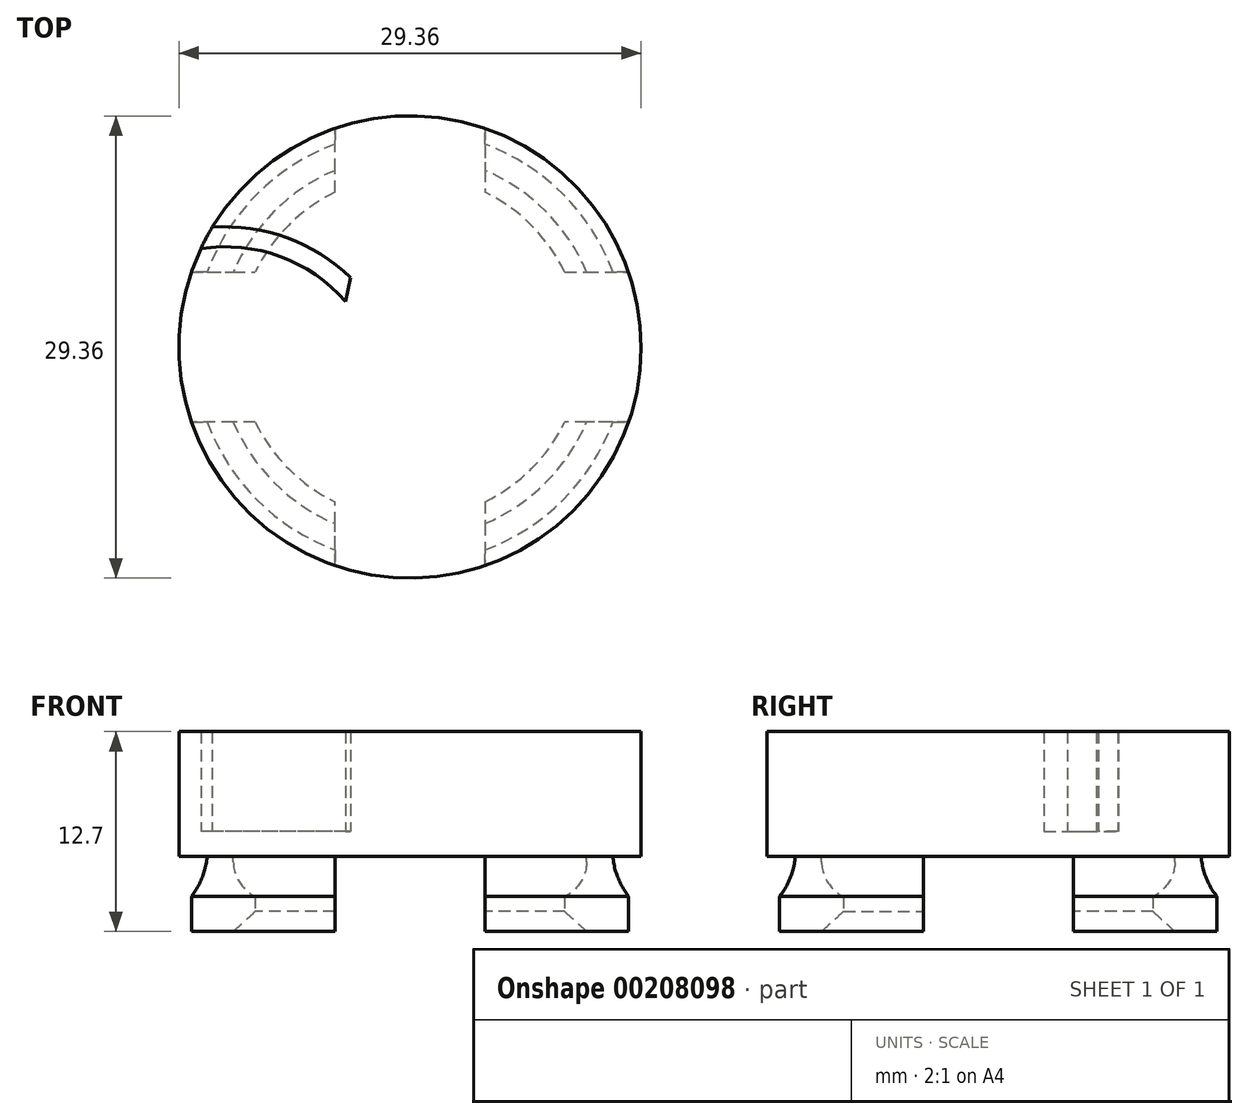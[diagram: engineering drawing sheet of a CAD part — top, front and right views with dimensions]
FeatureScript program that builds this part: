
annotation { "Feature Type Name" : "Feature", "Feature Type Description" : "" }
export const myFeature = defineFeature(function(context is Context, id is Id, definition is map)
    precondition{}
    {
        {
            var Q0;
            Q0=qCreatedBy(makeId("Top.planeOp"),FACE);
            var sketch = newSketch(context, id + "F0", { "sketchPlane" : qUnion([Q0])});
            skCircle(sketch, "E0", {"center": v(0, 0) * mm, "radius": 10.92 * mm});
            skCircle(sketch, "E1", {"center": v(0, 0) * mm, "radius": 14.68 * mm});
            skSolve(sketch);
        }
        {
            var Q0;
            Q0=makeQuery(id+"F0.imprint","IMPRINT",FACE,{"disambiguationData":[TD([[makeQuery(id+"F0.imprint","IMPRINT",EDGE,{"derivedFrom":sQuery(id+"F0.wireOp",EDGE,"E0")}),-1.0]])]});
            extrude(context, id + "F1", {"entities" : qUnion([Q0]), "depth" : 4.76 * mm});
        }
        {
            var Q0;
            Q0=makeQuery(id+"F1.opExtrude","CAP_FACE",FACE,{"disambiguationData":[OSD([sQuery(id+"F0.wireOp",EDGE,"E0"),sQuery(id+"F0.wireOp",EDGE,"E1")])],"isStart":false});
            var sketch = newSketch(context, id + "F2", { "sketchPlane" : qUnion([Q0])});
            skCircle(sketch, "E2", {"center": v(0, 0) * mm, "radius": 14.68 * mm});
            skSolve(sketch);
        }
        {
            var Q0;
            Q0 = qSketchRegion(id + "F2", true);
            extrude(context, id + "F3", {"entities" : qUnion([Q0]), "operationType" : NewBodyOperationType.ADD, "depth" : 1.59 * mm});
        }
        {
            var Q0;
            Q0=makeQuery(id+"F3.opExtrude","CAP_FACE",FACE,{"disambiguationData":[OSD([sQuery(id+"F2.wireOp",EDGE,"E2")])],"isStart":false});
            var sketch = newSketch(context, id + "F4", { "sketchPlane" : qUnion([Q0])});
            skLineSegment(sketch, "E3", {"start": v(1.24, 2.59) * mm, "end": v(-12.56, 7.6) * mm, "construction": true});
            skLineSegment(sketch, "E4", {"start": v(-14.5, -11.42) * mm, "end": v(-8.16, 6) * mm, "construction": true});
            skLineSegment(sketch, "E5", {"start": v(-13.28, 6.25) * mm, "end": v(-3.22, 2.59) * mm, "construction": true});
            skArc(sketch, "E6", {"start": v(-13.28, 6.25) * mm, "mid": v(-8.26, 5.76) * mm, "end": v(-4.09, 2.9) * mm});
            skArc(sketch, "E7", {"start": v(-12.56, 7.6) * mm, "mid": v(-7.82, 6.95) * mm, "end": v(-3.77, 4.41) * mm});
            skLineSegment(sketch, "E8", {"start": v(-4.09, 2.9) * mm, "end": v(-3.77, 4.41) * mm});
            skArc(sketch, "E9", {"start": v(-12.56, 7.6) * mm, "mid": v(-12.94, 6.94) * mm, "end": v(-13.28, 6.25) * mm});
            skSolve(sketch);
        }
        {
            var Q0;
            Q0=makeQuery(id+"F4.imprint","IMPRINT",FACE,{"disambiguationData":[TD([[makeQuery(id+"F4.imprint","IMPRINT",EDGE,{"derivedFrom":sQuery(id+"F4.wireOp",EDGE,"E6")}),1.0]])]});
            extrude(context, id + "F5", {"entities" : qUnion([Q0]), "operationType" : NewBodyOperationType.ADD, "depth" : 6.35 * mm});
        }
        {
            var Q0;
            Q0=qCreatedBy(makeId("Front.planeOp"),FACE);
            var sketch = newSketch(context, id + "F6", { "sketchPlane" : qUnion([Q0])});
            skLineSegment(sketch, "E10", {"start": v(0, 0) * mm, "end": v(0, 45.47) * mm, "construction": true});
            skSolve(sketch);
        }
        {
            var Q0;
            Q0=makeQuery(id+"F1.opExtrude","CAP_FACE",FACE,{"disambiguationData":[OSD([sQuery(id+"F0.wireOp",EDGE,"E0"),sQuery(id+"F0.wireOp",EDGE,"E1")])],"isStart":true});
            var sketch = newSketch(context, id + "F7", { "sketchPlane" : qUnion([Q0])});
            skLineSegment(sketch, "E11", {"start": v(-15.88, 4.76) * mm, "end": v(-15.88, -4.76) * mm});
            skLineSegment(sketch, "E12", {"start": v(-15.88, -4.76) * mm, "end": v(-4.76, -4.76) * mm});
            skLineSegment(sketch, "E13", {"start": v(-4.76, -4.76) * mm, "end": v(-4.76, -15.88) * mm});
            skLineSegment(sketch, "E14", {"start": v(-4.76, -15.88) * mm, "end": v(4.76, -15.88) * mm});
            skLineSegment(sketch, "E15", {"start": v(4.76, -15.88) * mm, "end": v(4.76, -4.76) * mm});
            skLineSegment(sketch, "E16", {"start": v(4.76, -4.76) * mm, "end": v(15.88, -4.76) * mm});
            skLineSegment(sketch, "E17", {"start": v(15.88, -4.76) * mm, "end": v(15.88, 4.76) * mm});
            skLineSegment(sketch, "E18", {"start": v(15.88, 4.76) * mm, "end": v(4.76, 4.76) * mm});
            skLineSegment(sketch, "E19", {"start": v(4.76, 4.76) * mm, "end": v(4.76, 15.88) * mm});
            skLineSegment(sketch, "E20", {"start": v(4.76, 15.87) * mm, "end": v(-4.76, 15.87) * mm});
            skLineSegment(sketch, "E21", {"start": v(-4.76, 15.88) * mm, "end": v(-4.76, 4.76) * mm});
            skLineSegment(sketch, "E22", {"start": v(-4.76, 4.76) * mm, "end": v(-15.88, 4.76) * mm});
            skLineSegment(sketch, "E23", {"start": v(0, 15.88) * mm, "end": v(0, -15.88) * mm, "construction": true});
            skLineSegment(sketch, "E24", {"start": v(-15.88, 0) * mm, "end": v(15.88, 0) * mm, "construction": true});
            skSolve(sketch);
        }
        {
            var Q0;
            Q0 = qSketchRegion(id + "F7", true);
            var Q1;
            Q1=makeQuery(id+"F3.opExtrude","CAP_FACE",FACE,{"disambiguationData":[OSD([sQuery(id+"F2.wireOp",EDGE,"E2")])],"isStart":true});
            extrude(context, id + "F8", {"entities" : qUnion([Q0]), "operationType" : NewBodyOperationType.REMOVE, "endBound" : BoundingType.UP_TO_SURFACE, "oppositeDirection" : true, "endBoundEntityFace" : qUnion([Q1]), "depth" : 25.4 * mm});
        }
        {
            var Q0;
            Q0=makeQuery(id+"F8.boolean.opBoolean","MERGE",FACE,{"derivedFrom":[makeQuery(id+"F3.opExtrude","CAP_FACE",FACE,{"disambiguationData":[OSD([sQuery(id+"F2.wireOp",EDGE,"E2")])],"isStart":true})],"fromTools":[makeQuery(id+"F8.opExtrude","CAP_FACE",FACE,{"disambiguationData":[OSD([sQuery(id+"F7.wireOp",EDGE,"E11"),sQuery(id+"F7.wireOp",EDGE,"E12"),sQuery(id+"F7.wireOp",EDGE,"E13"),sQuery(id+"F7.wireOp",EDGE,"E14"),sQuery(id+"F7.wireOp",EDGE,"E15"),sQuery(id+"F7.wireOp",EDGE,"E16"),sQuery(id+"F7.wireOp",EDGE,"E17"),sQuery(id+"F7.wireOp",EDGE,"E18"),sQuery(id+"F7.wireOp",EDGE,"E19"),sQuery(id+"F7.wireOp",EDGE,"E20"),sQuery(id+"F7.wireOp",EDGE,"E21"),sQuery(id+"F7.wireOp",EDGE,"E22")])],"isStart":false})]});
            var sketch = newSketch(context, id + "F9", { "sketchPlane" : qUnion([Q0])});
            skCircle(sketch, "E25", {"center": v(0, 0) * mm, "radius": 14.68 * mm});
            skCircle(sketch, "E26", {"center": v(0, 0) * mm, "radius": 13.72 * mm});
            skSolve(sketch);
        }
        {
            var Q0;
            Q0 = qSketchRegion(id + "F9", true);
            extrude(context, id + "F10", {"entities" : qUnion([Q0]), "operationType" : NewBodyOperationType.REMOVE, "depth" : 2.54 * mm});
        }
        {
            var Q0;
            {var subQ0=sQuery(id+"F9.wireOp",EDGE,"E26");Q0=makeQuery(id+"F10.boolean.opBoolean","COPY",EDGE,{"disambiguationData":[TD([makeQuery(id+"F8.boolean.opBoolean","COPY",FACE,{"derivedFrom":makeQuery(id+"F8.opExtrude","SWEPT_FACE",FACE,{"disambiguationData":[OSD([sQuery(id+"F7.wireOp",EDGE,"E18")])]})})])],"derivedFrom":makeQuery(id+"F10.opExtrude","CAP_EDGE",EDGE,{"disambiguationData":[OSD([subQ0])],"isStart":false})});}
            var Q1;
            {var subQ0=sQuery(id+"F9.wireOp",EDGE,"E26");Q1=makeQuery(id+"F10.boolean.opBoolean","COPY",EDGE,{"disambiguationData":[TD([makeQuery(id+"F8.boolean.opBoolean","COPY",FACE,{"derivedFrom":makeQuery(id+"F8.opExtrude","SWEPT_FACE",FACE,{"disambiguationData":[OSD([sQuery(id+"F7.wireOp",EDGE,"E15")])]})})])],"derivedFrom":makeQuery(id+"F10.opExtrude","CAP_EDGE",EDGE,{"disambiguationData":[OSD([subQ0])],"isStart":false})});}
            var Q2;
            {var subQ0=sQuery(id+"F9.wireOp",EDGE,"E26");Q2=makeQuery(id+"F10.boolean.opBoolean","COPY",EDGE,{"disambiguationData":[TD([makeQuery(id+"F8.boolean.opBoolean","COPY",FACE,{"derivedFrom":makeQuery(id+"F8.opExtrude","SWEPT_FACE",FACE,{"disambiguationData":[OSD([sQuery(id+"F7.wireOp",EDGE,"E12")])]})})])],"derivedFrom":makeQuery(id+"F10.opExtrude","CAP_EDGE",EDGE,{"disambiguationData":[OSD([subQ0])],"isStart":false})});}
            var Q3;
            {var subQ0=sQuery(id+"F9.wireOp",EDGE,"E26");Q3=makeQuery(id+"F10.boolean.opBoolean","COPY",EDGE,{"disambiguationData":[TD([makeQuery(id+"F8.boolean.opBoolean","COPY",FACE,{"derivedFrom":makeQuery(id+"F8.opExtrude","SWEPT_FACE",FACE,{"disambiguationData":[OSD([sQuery(id+"F7.wireOp",EDGE,"E21")])]})})])],"derivedFrom":makeQuery(id+"F10.opExtrude","CAP_EDGE",EDGE,{"disambiguationData":[OSD([subQ0])],"isStart":false})});}
            fillet(context, id + "F11", {"entities" : qUnion([Q0, Q1, Q2, Q3]), "radius" : 5.08 * mm, "tangentPropagation" : true, "allowEdgeOverflow" : false});
        }
        {
            var Q0;
            Q0=makeQuery(id+"F10.boolean.opBoolean","MERGE",FACE,{"derivedFrom":[makeQuery(id+"F8.boolean.opBoolean","MERGE",FACE,{"derivedFrom":[makeQuery(id+"F3.opExtrude","CAP_FACE",FACE,{"disambiguationData":[OSD([sQuery(id+"F2.wireOp",EDGE,"E2")])],"isStart":true})],"fromTools":[makeQuery(id+"F8.opExtrude","CAP_FACE",FACE,{"disambiguationData":[OSD([sQuery(id+"F7.wireOp",EDGE,"E11"),sQuery(id+"F7.wireOp",EDGE,"E12"),sQuery(id+"F7.wireOp",EDGE,"E13"),sQuery(id+"F7.wireOp",EDGE,"E14"),sQuery(id+"F7.wireOp",EDGE,"E15"),sQuery(id+"F7.wireOp",EDGE,"E16"),sQuery(id+"F7.wireOp",EDGE,"E17"),sQuery(id+"F7.wireOp",EDGE,"E18"),sQuery(id+"F7.wireOp",EDGE,"E19"),sQuery(id+"F7.wireOp",EDGE,"E20"),sQuery(id+"F7.wireOp",EDGE,"E21"),sQuery(id+"F7.wireOp",EDGE,"E22")])],"isStart":false})]})],"fromTools":[makeQuery(id+"F10.opExtrude","CAP_FACE",FACE,{"disambiguationData":[OSD([sQuery(id+"F9.wireOp",EDGE,"E25"),sQuery(id+"F9.wireOp",EDGE,"E26")])],"isStart":true})]});
            var sketch = newSketch(context, id + "F12", { "sketchPlane" : qUnion([Q0])});
            skCircle(sketch, "E27", {"center": v(0, 0) * mm, "radius": 10.92 * mm});
            skCircle(sketch, "E28", {"center": v(0, 0) * mm, "radius": 12.2 * mm});
            skSolve(sketch);
        }
        {
            var Q0;
            Q0 = qSketchRegion(id + "F12", true);
            extrude(context, id + "F13", {"entities" : qUnion([Q0]), "operationType" : NewBodyOperationType.REMOVE, "depth" : 2.54 * mm});
        }
        {
            var Q0;
            {var subQ0=sQuery(id+"F12.wireOp",EDGE,"E28");Q0=makeQuery(id+"F13.boolean.opBoolean","COPY",EDGE,{"disambiguationData":[TD([makeQuery(id+"F8.boolean.opBoolean","COPY",FACE,{"derivedFrom":makeQuery(id+"F8.opExtrude","SWEPT_FACE",FACE,{"disambiguationData":[OSD([sQuery(id+"F7.wireOp",EDGE,"E18")])]})})])],"derivedFrom":makeQuery(id+"F13.opExtrude","CAP_EDGE",EDGE,{"disambiguationData":[OSD([subQ0])],"isStart":false})});}
            var Q1;
            {var subQ0=sQuery(id+"F12.wireOp",EDGE,"E28");Q1=makeQuery(id+"F13.boolean.opBoolean","COPY",EDGE,{"disambiguationData":[TD([makeQuery(id+"F8.boolean.opBoolean","COPY",FACE,{"derivedFrom":makeQuery(id+"F8.opExtrude","SWEPT_FACE",FACE,{"disambiguationData":[OSD([sQuery(id+"F7.wireOp",EDGE,"E15")])]})})])],"derivedFrom":makeQuery(id+"F13.opExtrude","CAP_EDGE",EDGE,{"disambiguationData":[OSD([subQ0])],"isStart":false})});}
            var Q2;
            {var subQ0=sQuery(id+"F12.wireOp",EDGE,"E28");Q2=makeQuery(id+"F13.boolean.opBoolean","COPY",EDGE,{"disambiguationData":[TD([makeQuery(id+"F8.boolean.opBoolean","COPY",FACE,{"derivedFrom":makeQuery(id+"F8.opExtrude","SWEPT_FACE",FACE,{"disambiguationData":[OSD([sQuery(id+"F7.wireOp",EDGE,"E12")])]})})])],"derivedFrom":makeQuery(id+"F13.opExtrude","CAP_EDGE",EDGE,{"disambiguationData":[OSD([subQ0])],"isStart":false})});}
            var Q3;
            {var subQ0=sQuery(id+"F12.wireOp",EDGE,"E28");Q3=makeQuery(id+"F13.boolean.opBoolean","COPY",EDGE,{"disambiguationData":[TD([makeQuery(id+"F8.boolean.opBoolean","COPY",FACE,{"derivedFrom":makeQuery(id+"F8.opExtrude","SWEPT_FACE",FACE,{"disambiguationData":[OSD([sQuery(id+"F7.wireOp",EDGE,"E21")])]})})])],"derivedFrom":makeQuery(id+"F13.opExtrude","CAP_EDGE",EDGE,{"disambiguationData":[OSD([subQ0])],"isStart":false})});}
            fillet(context, id + "F14", {"entities" : qUnion([Q0, Q1, Q2, Q3]), "radius" : 2.54 * mm, "tangentPropagation" : true, "allowEdgeOverflow" : false});
        }
        {
            var Q0;
            {var subQ0=sQuery(id+"F0.wireOp",EDGE,"E0");Q0=makeQuery(id+"F8.boolean.opBoolean","SPLIT",EDGE,{"disambiguationData":[TD([makeQuery(id+"F8.opExtrude","SWEPT_FACE",FACE,{"disambiguationData":[OSD([sQuery(id+"F7.wireOp",EDGE,"E12")])]})])],"derivedFrom":makeQuery(id+"F1.opExtrude","CAP_EDGE",EDGE,{"disambiguationData":[OSD([subQ0])],"isStart":true})});}
            var Q1;
            {var subQ0=sQuery(id+"F0.wireOp",EDGE,"E0");Q1=makeQuery(id+"F8.boolean.opBoolean","SPLIT",EDGE,{"disambiguationData":[TD([makeQuery(id+"F8.opExtrude","SWEPT_FACE",FACE,{"disambiguationData":[OSD([sQuery(id+"F7.wireOp",EDGE,"E21")])]})])],"derivedFrom":makeQuery(id+"F1.opExtrude","CAP_EDGE",EDGE,{"disambiguationData":[OSD([subQ0])],"isStart":true})});}
            var Q2;
            {var subQ0=sQuery(id+"F0.wireOp",EDGE,"E0");Q2=makeQuery(id+"F8.boolean.opBoolean","SPLIT",EDGE,{"disambiguationData":[TD([makeQuery(id+"F8.opExtrude","SWEPT_FACE",FACE,{"disambiguationData":[OSD([sQuery(id+"F7.wireOp",EDGE,"E18")])]})])],"derivedFrom":makeQuery(id+"F1.opExtrude","CAP_EDGE",EDGE,{"disambiguationData":[OSD([subQ0])],"isStart":true})});}
            var Q3;
            {var subQ0=sQuery(id+"F0.wireOp",EDGE,"E0");Q3=makeQuery(id+"F8.boolean.opBoolean","SPLIT",EDGE,{"disambiguationData":[TD([makeQuery(id+"F8.opExtrude","SWEPT_FACE",FACE,{"disambiguationData":[OSD([sQuery(id+"F7.wireOp",EDGE,"E15")])]})])],"derivedFrom":makeQuery(id+"F1.opExtrude","CAP_EDGE",EDGE,{"disambiguationData":[OSD([subQ0])],"isStart":true})});}
            chamfer(context, id + "F15", {"entities" : qUnion([Q0, Q1, Q2, Q3]), "width" : 1.27 * mm, "tangentPropagation" : true});
        }
    });
